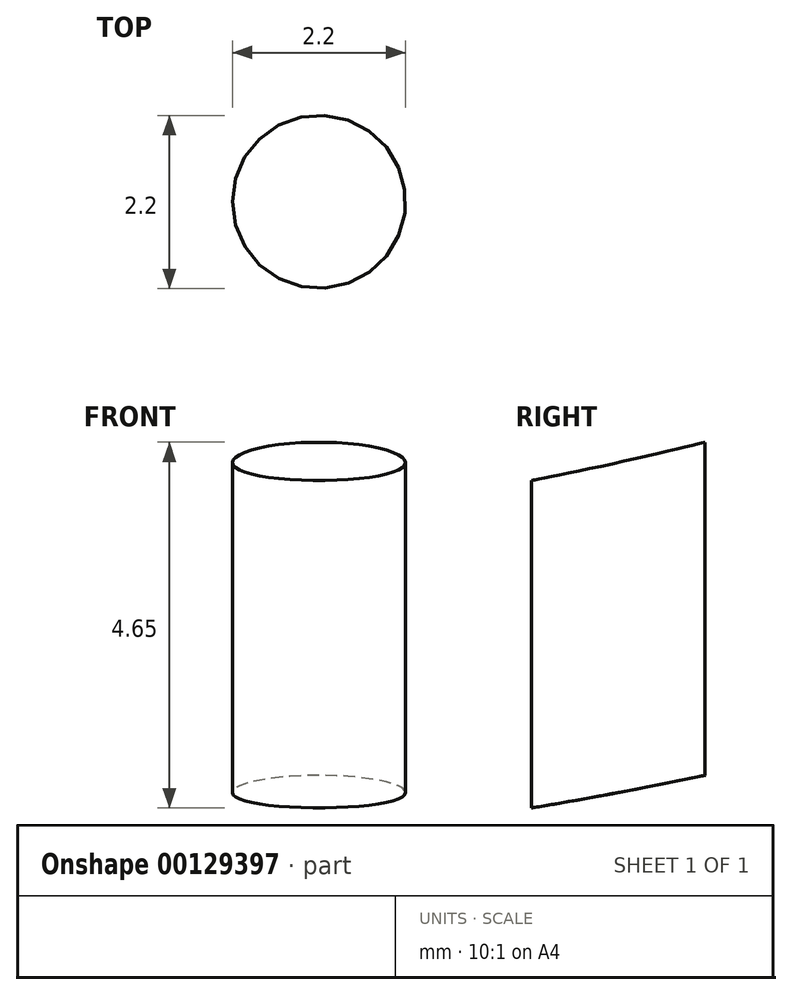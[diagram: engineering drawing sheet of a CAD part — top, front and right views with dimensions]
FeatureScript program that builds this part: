
annotation { "Feature Type Name" : "Feature", "Feature Type Description" : "" }
export const myFeature = defineFeature(function(context is Context, id is Id, definition is map)
    precondition{}
    {
        {
            var Q0;
            Q0=qCreatedBy(makeId("Front.planeOp"),FACE);
            var sketch = newSketch(context, id + "F0", { "sketchPlane" : qUnion([Q0])});
            skEllipticalArc(sketch, "E0", {});
            skLineSegment(sketch, "E1", {"start": v(0, 77.97) * mm, "end": v(0, -78.82) * mm, "construction": true});
            skLineSegment(sketch, "E2", {"start": v(105.1, 0) * mm, "end": v(-114.38, 0) * mm, "construction": true});
            skFitSpline(sketch, "E3.0", {"points": [v(79.4, -1.95) * mm, v(79.54, 0) * mm, v(79.4, 1.95) * mm, v(78.86, 4.5) * mm, v(77.58, 7.49) * mm, v(75.25, 10.7) * mm, v(72.28, 13.61) * mm, v(68.71, 16.27) * mm, v(64.56, 18.7) * mm, v(60.64, 20.57) * mm, v(57.22, 21.96) * mm, v(54.52, 22.96) * mm, v(51.7, 23.9) * mm, v(47.8, 25.09) * mm, v(42.67, 26.42) * mm, v(36.18, 27.79) * mm, v(29.38, 28.92) * mm, v(22.31, 29.8) * mm, v(16.25, 30.34) * mm, v(11.31, 30.65) * mm, v(7.57, 30.81) * mm, v(3.8, 30.91) * mm, v(0, 30.94) * mm, v(-3.8, 30.91) * mm, v(-7.57, 30.81) * mm, v(-11.31, 30.65) * mm, v(-16.25, 30.34) * mm, v(-22.31, 29.8) * mm, v(-29.38, 28.92) * mm, v(-36.18, 27.79) * mm, v(-42.67, 26.42) * mm, v(-47.8, 25.09) * mm, v(-51.7, 23.9) * mm, v(-54.52, 22.96) * mm, v(-57.22, 21.96) * mm, v(-60.64, 20.57) * mm, v(-64.56, 18.7) * mm, v(-68.71, 16.27) * mm, v(-72.28, 13.61) * mm, v(-75.25, 10.7) * mm, v(-77.58, 7.49) * mm, v(-78.86, 4.5) * mm, v(-79.4, 1.95) * mm, v(-79.54, 0) * mm, v(-79.4, -1.95) * mm, v(-78.86, -4.5) * mm, v(-77.58, -7.49) * mm, v(-75.25, -10.7) * mm, v(-72.28, -13.61) * mm, v(-68.71, -16.27) * mm, v(-64.56, -18.7) * mm, v(-60.64, -20.57) * mm, v(-57.22, -21.96) * mm, v(-54.52, -22.96) * mm, v(-51.7, -23.9) * mm, v(-47.8, -25.09) * mm, v(-42.67, -26.42) * mm, v(-36.18, -27.79) * mm, v(-29.38, -28.92) * mm, v(-22.31, -29.8) * mm, v(-16.25, -30.34) * mm, v(-11.31, -30.65) * mm, v(-7.57, -30.81) * mm, v(-3.8, -30.91) * mm, v(0, -30.94) * mm, v(3.8, -30.91) * mm, v(7.57, -30.81) * mm, v(11.31, -30.65) * mm, v(16.25, -30.34) * mm, v(22.31, -29.8) * mm, v(29.38, -28.92) * mm, v(36.18, -27.79) * mm, v(42.67, -26.42) * mm, v(47.8, -25.09) * mm, v(51.7, -23.9) * mm, v(54.52, -22.96) * mm, v(57.22, -21.96) * mm, v(60.64, -20.57) * mm, v(64.56, -18.7) * mm, v(68.71, -16.27) * mm, v(72.28, -13.61) * mm, v(75.25, -10.7) * mm, v(77.58, -7.49) * mm, v(78.86, -4.5) * mm, v(79.4, -1.95) * mm, v(79.54, 0) * mm, v(79.4, 1.95) * mm]});
            skLineSegment(sketch, "E4", {"start": v(0, 26.36) * mm, "end": v(0, 30.93) * mm});
            skLineSegment(sketch, "E5", {"start": v(76.37, 9.1) * mm, "end": v(83.95, 3.01) * mm});
            skLineSegment(sketch, "E6", {"start": v(92.04, 2.1) * mm, "end": v(100.76, 6.3) * mm});
            skLineSegment(sketch, "E7", {"start": v(100.76, 6.3) * mm, "end": v(101.6, 4.57) * mm});
            skLineSegment(sketch, "E8", {"start": v(99.24, -2.2) * mm, "end": v(92.47, -5.48) * mm});
            skLineSegment(sketch, "E9", {"start": v(83.88, -4.11) * mm, "end": v(72.04, 7.24) * mm});
            skFitSpline(sketch, "E10.trimOffspring", {"points": [v(79.4, -1.95) * mm, v(79.54, 0) * mm, v(79.4, 1.95) * mm, v(78.86, 4.5) * mm, v(77.58, 7.49) * mm, v(75.25, 10.7) * mm, v(72.28, 13.61) * mm, v(68.71, 16.27) * mm, v(64.56, 18.7) * mm, v(60.64, 20.57) * mm, v(57.22, 21.96) * mm, v(54.52, 22.96) * mm, v(51.7, 23.9) * mm, v(47.8, 25.09) * mm, v(42.67, 26.42) * mm, v(36.18, 27.79) * mm, v(29.38, 28.92) * mm, v(22.31, 29.8) * mm, v(16.25, 30.34) * mm, v(11.31, 30.65) * mm, v(7.57, 30.81) * mm, v(3.8, 30.91) * mm, v(0, 30.94) * mm, v(-3.8, 30.91) * mm, v(-7.57, 30.81) * mm, v(-11.31, 30.65) * mm, v(-16.25, 30.34) * mm, v(-22.31, 29.8) * mm, v(-29.38, 28.92) * mm, v(-36.18, 27.79) * mm, v(-42.67, 26.42) * mm, v(-47.8, 25.09) * mm, v(-51.7, 23.9) * mm, v(-54.52, 22.96) * mm, v(-57.22, 21.96) * mm, v(-60.64, 20.57) * mm, v(-64.56, 18.7) * mm, v(-68.71, 16.27) * mm, v(-72.28, 13.61) * mm, v(-75.25, 10.7) * mm, v(-77.58, 7.49) * mm, v(-78.86, 4.5) * mm, v(-79.4, 1.95) * mm, v(-79.54, 0) * mm, v(-79.4, -1.95) * mm, v(-78.86, -4.5) * mm, v(-77.58, -7.49) * mm, v(-75.25, -10.7) * mm, v(-72.28, -13.61) * mm, v(-68.71, -16.27) * mm, v(-64.56, -18.7) * mm, v(-60.64, -20.57) * mm, v(-57.22, -21.96) * mm, v(-54.52, -22.96) * mm, v(-51.7, -23.9) * mm, v(-47.8, -25.09) * mm, v(-42.67, -26.42) * mm, v(-36.18, -27.79) * mm, v(-29.38, -28.92) * mm, v(-22.31, -29.8) * mm, v(-16.25, -30.34) * mm, v(-11.31, -30.65) * mm, v(-7.57, -30.81) * mm, v(-3.8, -30.91) * mm, v(0, -30.94) * mm, v(3.8, -30.91) * mm, v(7.57, -30.81) * mm, v(11.31, -30.65) * mm, v(16.25, -30.34) * mm, v(22.31, -29.8) * mm, v(29.38, -28.92) * mm, v(36.18, -27.79) * mm, v(42.67, -26.42) * mm, v(47.8, -25.09) * mm, v(51.7, -23.9) * mm, v(54.52, -22.96) * mm, v(57.22, -21.96) * mm, v(60.64, -20.57) * mm, v(64.56, -18.7) * mm, v(68.71, -16.27) * mm, v(72.28, -13.61) * mm, v(75.25, -10.7) * mm, v(77.58, -7.49) * mm, v(78.86, -4.5) * mm, v(79.4, -1.95) * mm, v(79.54, 0) * mm, v(79.4, 1.95) * mm]});
            skPoint(sketch, "E11.visualSharp", {"position": v(87.7, 0) * mm});
            skArc(sketch, "E11.filletArc", {"start": v(83.95, 3.01) * mm, "mid": v(87.86, 1.38) * mm, "end": v(92.04, 2.1) * mm});
            skPoint(sketch, "E12.visualSharp", {"position": v(87.7, -7.78) * mm});
            skArc(sketch, "E12.filletArc", {"start": v(83.88, -4.11) * mm, "mid": v(87.96, -6.14) * mm, "end": v(92.47, -5.48) * mm});
            skPoint(sketch, "E13.visualSharp", {"position": v(103.8, 0) * mm});
            skArc(sketch, "E13.filletArc", {"start": v(99.24, -2.2) * mm, "mid": v(101.82, 0.7) * mm, "end": v(101.6, 4.57) * mm});
            const initialGuessF0  = {"E0": [0, 0, 1, 0, 0.07492573200211738, 0.026360478493963616, 0.27833524355657596, 1.5707963267948966]};
            skSetInitialGuess(sketch, initialGuessF0);
            skSolve(sketch);
        }
        {
            var Q0;
            Q0=qCreatedBy(makeId("Top.planeOp"),FACE);
            var sketch = newSketch(context, id + "F1", { "sketchPlane" : qUnion([Q0])});
            skCircle(sketch, "E14", {"center": v(42, 41.86) * mm, "radius": 33.02 * mm});
            skCircle(sketch, "E15", {"center": v(41.05, -41.44) * mm, "radius": 33.02 * mm});
            skCircle(sketch, "E16", {"center": v(-43.3, -41.58) * mm, "radius": 33.02 * mm});
            skCircle(sketch, "E17", {"center": v(-42.93, 41.43) * mm, "radius": 33.02 * mm});
            skSolve(sketch);
        }
        {
            var Q0;
            Q0=qCreatedBy(makeId("Front.planeOp"),FACE);
            var sketch = newSketch(context, id + "F7", { "sketchPlane" : qUnion([Q0])});
            skFitSpline(sketch, "E18", {"points": [v(1.72, 46.54) * mm, v(55.15, 43.98) * mm, v(92.23, 22.98) * mm, v(113.08, 26.47) * mm, v(119.36, 26.47) * mm, v(92.15, 18.5) * mm, v(53.46, 38.66) * mm, v(5.04, 43.2) * mm, v(1.72, 46.54) * mm]});
            skSolve(sketch);
        }
        {
            var Q0;
            Q0=makeQuery(id+"F7.imprint","IMPRINT",FACE,{"disambiguationData":[TD([[makeQuery(id+"F7.imprint","IMPRINT",EDGE,{"derivedFrom":sQuery(id+"F7.wireOp",EDGE,"E18")}),-1.0]])]});
            var Q1;
            Q1=sQuery(id+"F0.wireOp",EDGE,"E1");
            revolve(context, id + "F8", {"entities" : qUnion([Q0]), "axis" : qUnion([Q1]), "revolveType" : RevolveType.FULL});
        }
        {
            var Q0;
            Q0=makeQuery(id+"F1.imprint","IMPRINT",FACE,{"disambiguationData":[TD([[makeQuery(id+"F1.imprint","IMPRINT",EDGE,{"derivedFrom":sQuery(id+"F1.wireOp",EDGE,"E15")}),1.0]])]});
            var Q1;
            Q1=makeQuery(id+"F1.imprint","IMPRINT",FACE,{"disambiguationData":[TD([[makeQuery(id+"F1.imprint","IMPRINT",EDGE,{"derivedFrom":sQuery(id+"F1.wireOp",EDGE,"E16")}),1.0]])]});
            var Q2;
            Q2=makeQuery(id+"F1.imprint","IMPRINT",FACE,{"disambiguationData":[TD([[makeQuery(id+"F1.imprint","IMPRINT",EDGE,{"derivedFrom":sQuery(id+"F1.wireOp",EDGE,"E17")}),1.0]])]});
            var Q3;
            Q3=makeQuery(id+"F1.imprint","IMPRINT",FACE,{"disambiguationData":[TD([[makeQuery(id+"F1.imprint","IMPRINT",EDGE,{"derivedFrom":sQuery(id+"F1.wireOp",EDGE,"E14")}),1.0]])]});
            var Q4;
            Q4=sQuery(id+"F1.wireOp",EDGE,"E14");
            var Q5;
            Q5=sQuery(id+"F1.wireOp",EDGE,"E15");
            var Q6;
            Q6=sQuery(id+"F1.wireOp",EDGE,"E16");
            var Q7;
            Q7=sQuery(id+"F1.wireOp",EDGE,"E17");
            extrude(context, id + "F2", {"entities" : qUnion([Q0, Q1, Q2, Q3]), "operationType" : NewBodyOperationType.REMOVE, "surfaceEntities" : qUnion([Q4, Q5, Q6, Q7]), "depth" : 87.2 * mm});
        }
        {
            var Q0;
            Q0=qCreatedBy(makeId("Top.planeOp"),FACE);
            var sketch = newSketch(context, id + "F9", { "sketchPlane" : qUnion([Q0])});
            skCircle(sketch, "E19", {"center": v(0, 101.75) * mm, "radius": 4.99 * mm});
            skCircle(sketch, "E20", {"center": v(0, 101.75) * mm, "radius": 1.1 * mm});
            skPoint(sketch, "E21.center", {"position": v(0, 0) * mm});
            skLineSegment(sketch, "E21.anchor1", {"start": v(0, 0) * mm, "end": v(0, 101.75) * mm, "construction": true});
            skLineSegment(sketch, "E21.anchor2", {"start": v(0, 0) * mm, "end": v(0, 101.75) * mm, "construction": true});
            skCircle(sketch, "E22.1.0", {"center": v(-21.16, 99.53) * mm, "radius": 4.99 * mm});
            skCircle(sketch, "E22.1.1", {"center": v(-21.16, 99.53) * mm, "radius": 4.99 * mm});
            skCircle(sketch, "E22.1.2", {"center": v(-21.16, 99.53) * mm, "radius": 4.99 * mm});
            skCircle(sketch, "E22.2.0", {"center": v(-41.39, 92.96) * mm, "radius": 4.99 * mm});
            skCircle(sketch, "E22.2.1", {"center": v(-41.39, 92.96) * mm, "radius": 4.99 * mm});
            skCircle(sketch, "E22.2.2", {"center": v(-41.39, 92.96) * mm, "radius": 4.99 * mm});
            skCircle(sketch, "E23.1.3.0", {"center": v(-59.8, 82.32) * mm, "radius": 4.99 * mm});
            skCircle(sketch, "E23.2.3.0", {"center": v(-59.8, 82.32) * mm, "radius": 4.99 * mm});
            skCircle(sketch, "E23.4.3.0", {"center": v(-59.8, 82.32) * mm, "radius": 4.99 * mm});
            skCircle(sketch, "E23.1.4.0", {"center": v(-75.62, 68.09) * mm, "radius": 4.99 * mm});
            skCircle(sketch, "E23.2.4.0", {"center": v(-75.62, 68.09) * mm, "radius": 4.99 * mm});
            skCircle(sketch, "E23.4.4.0", {"center": v(-75.62, 68.09) * mm, "radius": 4.99 * mm});
            skCircle(sketch, "E23.1.5.0", {"center": v(-88.12, 50.88) * mm, "radius": 4.99 * mm});
            skCircle(sketch, "E23.2.5.0", {"center": v(-88.12, 50.88) * mm, "radius": 4.99 * mm});
            skCircle(sketch, "E23.4.5.0", {"center": v(-88.12, 50.88) * mm, "radius": 4.99 * mm});
            skCircle(sketch, "E23.1.6.0", {"center": v(-96.77, 31.44) * mm, "radius": 4.99 * mm});
            skCircle(sketch, "E23.2.6.0", {"center": v(-96.77, 31.44) * mm, "radius": 4.99 * mm});
            skCircle(sketch, "E23.4.6.0", {"center": v(-96.77, 31.44) * mm, "radius": 4.99 * mm});
            skCircle(sketch, "E23.1.7.0", {"center": v(-101.2, 10.64) * mm, "radius": 4.99 * mm});
            skCircle(sketch, "E23.2.7.0", {"center": v(-101.2, 10.64) * mm, "radius": 4.99 * mm});
            skCircle(sketch, "E23.4.7.0", {"center": v(-101.2, 10.64) * mm, "radius": 4.99 * mm});
            skCircle(sketch, "E23.1.8.0", {"center": v(-101.2, -10.64) * mm, "radius": 4.99 * mm});
            skCircle(sketch, "E23.2.8.0", {"center": v(-101.2, -10.64) * mm, "radius": 4.99 * mm});
            skCircle(sketch, "E23.4.8.0", {"center": v(-101.2, -10.64) * mm, "radius": 4.99 * mm});
            skCircle(sketch, "E23.1.9.0", {"center": v(-96.77, -31.44) * mm, "radius": 4.99 * mm});
            skCircle(sketch, "E23.2.9.0", {"center": v(-96.77, -31.44) * mm, "radius": 4.99 * mm});
            skCircle(sketch, "E23.4.9.0", {"center": v(-96.77, -31.44) * mm, "radius": 4.99 * mm});
            skCircle(sketch, "E23.1.10.0", {"center": v(-88.12, -50.88) * mm, "radius": 4.99 * mm});
            skCircle(sketch, "E23.2.10.0", {"center": v(-88.12, -50.88) * mm, "radius": 4.99 * mm});
            skCircle(sketch, "E23.4.10.0", {"center": v(-88.12, -50.88) * mm, "radius": 4.99 * mm});
            skCircle(sketch, "E23.1.11.0", {"center": v(-75.62, -68.09) * mm, "radius": 4.99 * mm});
            skCircle(sketch, "E23.2.11.0", {"center": v(-75.62, -68.09) * mm, "radius": 4.99 * mm});
            skCircle(sketch, "E23.4.11.0", {"center": v(-75.62, -68.09) * mm, "radius": 4.99 * mm});
            skCircle(sketch, "E23.1.12.0", {"center": v(-59.8, -82.32) * mm, "radius": 4.99 * mm});
            skCircle(sketch, "E23.2.12.0", {"center": v(-59.8, -82.32) * mm, "radius": 4.99 * mm});
            skCircle(sketch, "E23.4.12.0", {"center": v(-59.8, -82.32) * mm, "radius": 4.99 * mm});
            skCircle(sketch, "E23.1.13.0", {"center": v(-41.39, -92.96) * mm, "radius": 4.99 * mm});
            skCircle(sketch, "E23.2.13.0", {"center": v(-41.39, -92.96) * mm, "radius": 4.99 * mm});
            skCircle(sketch, "E23.4.13.0", {"center": v(-41.39, -92.96) * mm, "radius": 4.99 * mm});
            skCircle(sketch, "E23.1.14.0", {"center": v(-21.16, -99.53) * mm, "radius": 4.99 * mm});
            skCircle(sketch, "E23.2.14.0", {"center": v(-21.16, -99.53) * mm, "radius": 4.99 * mm});
            skCircle(sketch, "E23.4.14.0", {"center": v(-21.16, -99.53) * mm, "radius": 4.99 * mm});
            skCircle(sketch, "E23.1.15.0", {"center": v(0, -101.75) * mm, "radius": 4.99 * mm});
            skCircle(sketch, "E23.2.15.0", {"center": v(0, -101.75) * mm, "radius": 4.99 * mm});
            skCircle(sketch, "E23.4.15.0", {"center": v(0, -101.75) * mm, "radius": 4.99 * mm});
            skCircle(sketch, "E23.1.16.0", {"center": v(21.16, -99.53) * mm, "radius": 4.99 * mm});
            skCircle(sketch, "E23.2.16.0", {"center": v(21.16, -99.53) * mm, "radius": 4.99 * mm});
            skCircle(sketch, "E23.4.16.0", {"center": v(21.16, -99.53) * mm, "radius": 4.99 * mm});
            skCircle(sketch, "E23.1.17.0", {"center": v(41.39, -92.96) * mm, "radius": 4.99 * mm});
            skCircle(sketch, "E23.2.17.0", {"center": v(41.39, -92.96) * mm, "radius": 4.99 * mm});
            skCircle(sketch, "E23.4.17.0", {"center": v(41.39, -92.96) * mm, "radius": 4.99 * mm});
            skCircle(sketch, "E23.1.18.0", {"center": v(59.8, -82.32) * mm, "radius": 4.99 * mm});
            skCircle(sketch, "E23.2.18.0", {"center": v(59.8, -82.32) * mm, "radius": 4.99 * mm});
            skCircle(sketch, "E23.4.18.0", {"center": v(59.8, -82.32) * mm, "radius": 4.99 * mm});
            skCircle(sketch, "E23.1.19.0", {"center": v(75.62, -68.09) * mm, "radius": 4.99 * mm});
            skCircle(sketch, "E23.2.19.0", {"center": v(75.62, -68.09) * mm, "radius": 4.99 * mm});
            skCircle(sketch, "E23.4.19.0", {"center": v(75.62, -68.09) * mm, "radius": 4.99 * mm});
            skCircle(sketch, "E23.1.20.0", {"center": v(88.12, -50.88) * mm, "radius": 4.99 * mm});
            skCircle(sketch, "E23.2.20.0", {"center": v(88.12, -50.88) * mm, "radius": 4.99 * mm});
            skCircle(sketch, "E23.4.20.0", {"center": v(88.12, -50.88) * mm, "radius": 4.99 * mm});
            skCircle(sketch, "E23.1.21.0", {"center": v(96.77, -31.44) * mm, "radius": 4.99 * mm});
            skCircle(sketch, "E23.2.21.0", {"center": v(96.77, -31.44) * mm, "radius": 4.99 * mm});
            skCircle(sketch, "E23.4.21.0", {"center": v(96.77, -31.44) * mm, "radius": 4.99 * mm});
            skCircle(sketch, "E23.1.22.0", {"center": v(101.2, -10.64) * mm, "radius": 4.99 * mm});
            skCircle(sketch, "E23.2.22.0", {"center": v(101.2, -10.64) * mm, "radius": 4.99 * mm});
            skCircle(sketch, "E23.4.22.0", {"center": v(101.2, -10.64) * mm, "radius": 4.99 * mm});
            skCircle(sketch, "E23.1.23.0", {"center": v(101.2, 10.64) * mm, "radius": 4.99 * mm});
            skCircle(sketch, "E23.2.23.0", {"center": v(101.2, 10.64) * mm, "radius": 4.99 * mm});
            skCircle(sketch, "E23.4.23.0", {"center": v(101.2, 10.64) * mm, "radius": 4.99 * mm});
            skCircle(sketch, "E23.1.24.0", {"center": v(96.77, 31.44) * mm, "radius": 4.99 * mm});
            skCircle(sketch, "E23.2.24.0", {"center": v(96.77, 31.44) * mm, "radius": 4.99 * mm});
            skCircle(sketch, "E23.4.24.0", {"center": v(96.77, 31.44) * mm, "radius": 4.99 * mm});
            skCircle(sketch, "E23.1.25.0", {"center": v(88.12, 50.88) * mm, "radius": 4.99 * mm});
            skCircle(sketch, "E23.2.25.0", {"center": v(88.12, 50.88) * mm, "radius": 4.99 * mm});
            skCircle(sketch, "E23.4.25.0", {"center": v(88.12, 50.88) * mm, "radius": 4.99 * mm});
            skCircle(sketch, "E23.1.26.0", {"center": v(75.62, 68.09) * mm, "radius": 4.99 * mm});
            skCircle(sketch, "E23.2.26.0", {"center": v(75.62, 68.09) * mm, "radius": 4.99 * mm});
            skCircle(sketch, "E23.4.26.0", {"center": v(75.62, 68.09) * mm, "radius": 4.99 * mm});
            skCircle(sketch, "E23.1.27.0", {"center": v(59.8, 82.32) * mm, "radius": 4.99 * mm});
            skCircle(sketch, "E23.2.27.0", {"center": v(59.8, 82.32) * mm, "radius": 4.99 * mm});
            skCircle(sketch, "E23.4.27.0", {"center": v(59.8, 82.32) * mm, "radius": 4.99 * mm});
            skCircle(sketch, "E23.1.28.0", {"center": v(41.39, 92.96) * mm, "radius": 4.99 * mm});
            skCircle(sketch, "E23.2.28.0", {"center": v(41.39, 92.96) * mm, "radius": 4.99 * mm});
            skCircle(sketch, "E23.4.28.0", {"center": v(41.39, 92.96) * mm, "radius": 4.99 * mm});
            skCircle(sketch, "E23.1.29.0", {"center": v(21.16, 99.53) * mm, "radius": 4.99 * mm});
            skCircle(sketch, "E23.2.29.0", {"center": v(21.16, 99.53) * mm, "radius": 4.99 * mm});
            skCircle(sketch, "E23.4.29.0", {"center": v(21.16, 99.53) * mm, "radius": 4.99 * mm});
            skSolve(sketch);
        }
        {
            var Q0;
            Q0 = qSketchRegion(id + "F9", true);
            extrude(context, id + "F3", {"entities" : qUnion([Q0]), "operationType" : NewBodyOperationType.REMOVE, "depth" : 80.12 * mm});
        }
        {
            var Q0;
            Q0=qCreatedBy(makeId("Top.planeOp"),FACE);
            cPlane(context, id + "F4", {"entities" : qUnion([Q0]), "cplaneType" : CPlaneType.OFFSET, "offset" : 25.4 * mm, "width" : 152.4 * mm, "height" : 152.4 * mm});
        }
        {
            var Q0;
            Q0=qCreatedBy(id+"F4.planeOp",FACE);
            var sketch = newSketch(context, id + "F10", { "sketchPlane" : qUnion([Q0])});
            skLineSegment(sketch, "E24.bottom", {"start": v(-2, 94.24) * mm, "end": v(1.08, 94.24) * mm});
            skLineSegment(sketch, "E24.top", {"start": v(-2, -93.27) * mm, "end": v(1.08, -93.27) * mm});
            skLineSegment(sketch, "E24.left", {"start": v(-2, 94.24) * mm, "end": v(-2, -93.27) * mm});
            skLineSegment(sketch, "E24.right", {"start": v(1.08, 94.24) * mm, "end": v(1.08, -93.27) * mm});
            skLineSegment(sketch, "E25.bottom", {"start": v(-2, 94.24) * mm, "end": v(-2, 94.24) * mm});
            skLineSegment(sketch, "E25.top", {"start": v(-2, 94.24) * mm, "end": v(-2, 94.24) * mm});
            skLineSegment(sketch, "E25.left", {"start": v(-2, 94.24) * mm, "end": v(-2, 94.24) * mm});
            skLineSegment(sketch, "E25.right", {"start": v(-2, 94.24) * mm, "end": v(-2, 94.24) * mm});
            skLineSegment(sketch, "E26.bottom", {"start": v(-94.3, 1.13) * mm, "end": v(95.66, 1.13) * mm});
            skLineSegment(sketch, "E26.top", {"start": v(-94.3, -1.06) * mm, "end": v(95.66, -1.06) * mm});
            skLineSegment(sketch, "E26.left", {"start": v(-94.3, 1.13) * mm, "end": v(-94.3, -1.06) * mm});
            skLineSegment(sketch, "E26.right", {"start": v(95.66, 1.13) * mm, "end": v(95.66, -1.06) * mm});
            skSolve(sketch);
        }
        {
            var Q0;
            Q0 = qSketchRegion(id + "F10", true);
            extrude(context, id + "F5", {"entities" : qUnion([Q0]), "operationType" : NewBodyOperationType.REMOVE, "depth" : 42.4 * mm});
        }
        {
            var Q0;
            Q0=qCreatedBy(id+"F4.planeOp",FACE);
            var sketch = newSketch(context, id + "F6", { "sketchPlane" : qUnion([Q0])});
            skCircle(sketch, "E27", {"center": v(10.2, 9.9) * mm, "radius": 6.79 * mm});
            skCircle(sketch, "E28", {"center": v(10.2, -10.83) * mm, "radius": 6.4 * mm});
            skCircle(sketch, "E29", {"center": v(-10.9, -10.83) * mm, "radius": 6.66 * mm});
            skCircle(sketch, "E30", {"center": v(-10.9, 9.9) * mm, "radius": 6.72 * mm});
            skSolve(sketch);
        }
        {
            var Q0;
            Q0 = qSketchRegion(id + "F6", true);
            extrude(context, id + "F11", {"entities" : qUnion([Q0]), "operationType" : NewBodyOperationType.REMOVE, "depth" : 34.63 * mm});
        }
    });
